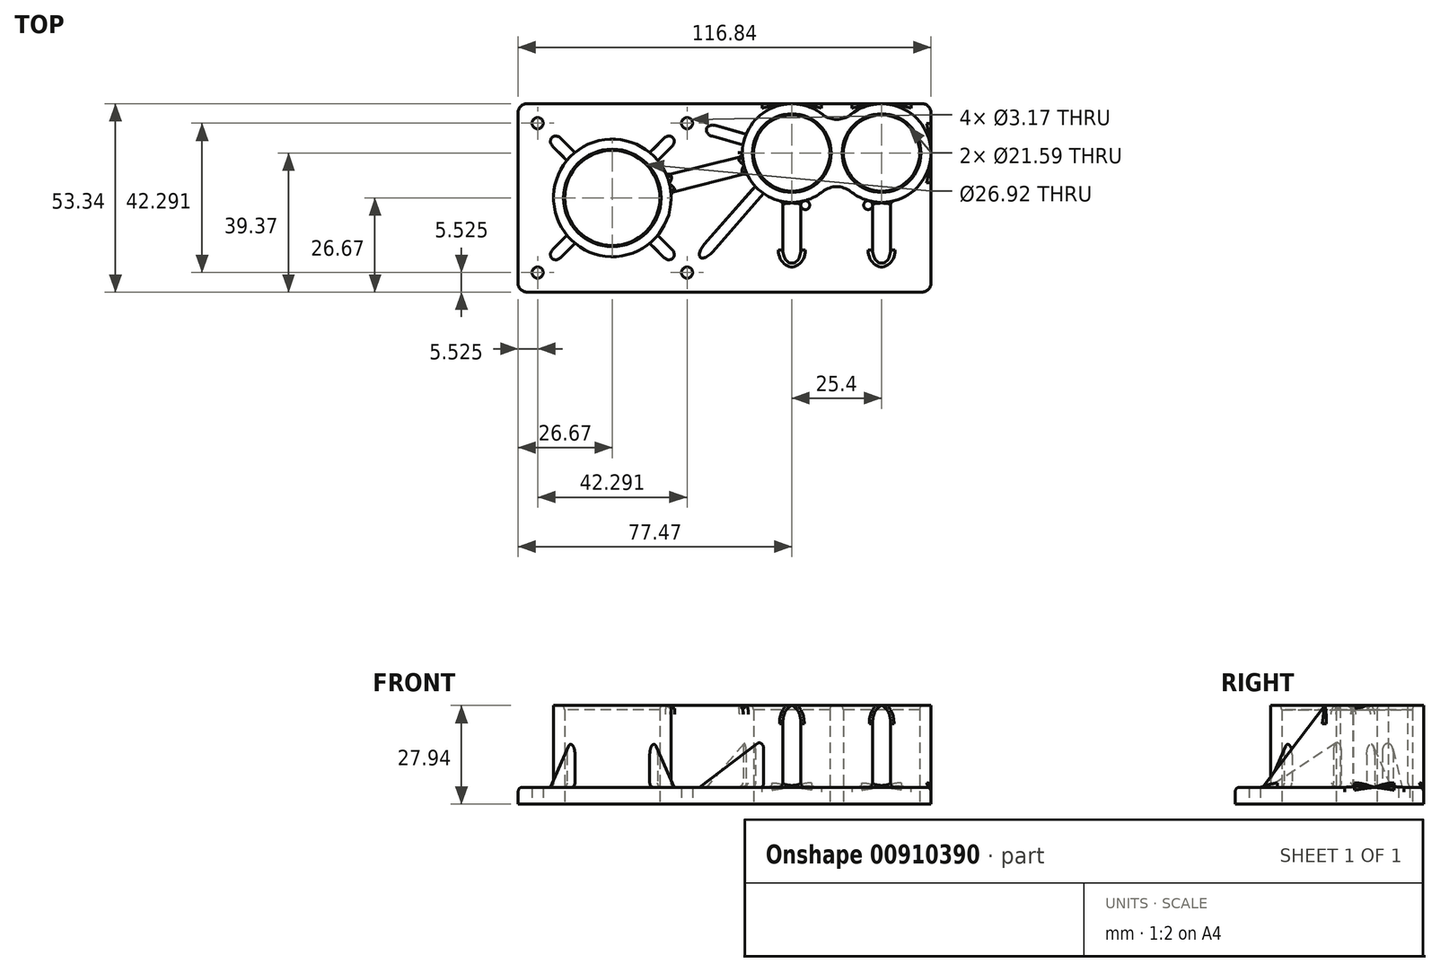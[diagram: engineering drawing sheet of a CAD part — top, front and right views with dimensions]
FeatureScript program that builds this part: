
annotation { "Feature Type Name" : "Feature", "Feature Type Description" : "" }
export const myFeature = defineFeature(function(context is Context, id is Id, definition is map)
    precondition{}
    {
        {
            var Q0;
            Q0=qCreatedBy(makeId("Top.planeOp"),FACE);
            var sketch = newSketch(context, id + "F0", { "sketchPlane" : qUnion([Q0])});
            skCircle(sketch, "E0", {"center": v(0, 0) * mm, "radius": 13.46 * mm});
            skLineSegment(sketch, "E1.bottom", {"start": v(-26.67, 26.67) * mm, "end": v(90.17, 26.67) * mm});
            skLineSegment(sketch, "E1.top", {"start": v(-26.67, -26.67) * mm, "end": v(90.17, -26.67) * mm});
            skLineSegment(sketch, "E1.left", {"start": v(-26.67, 26.67) * mm, "end": v(-26.67, -26.67) * mm});
            skLineSegment(sketch, "E1.right", {"start": v(90.17, 26.67) * mm, "end": v(90.17, -26.67) * mm});
            skCircle(sketch, "E2", {"center": v(50.8, 12.7) * mm, "radius": 10.8 * mm});
            skCircle(sketch, "E3", {"center": v(76.2, 12.7) * mm, "radius": 10.8 * mm});
            skCircle(sketch, "E4", {"center": v(-21.15, 21.15) * mm, "radius": 1.59 * mm});
            skCircle(sketch, "E5", {"center": v(21.15, 21.15) * mm, "radius": 1.59 * mm});
            skCircle(sketch, "E6", {"center": v(21.15, -21.15) * mm, "radius": 1.59 * mm});
            skCircle(sketch, "E7", {"center": v(-21.15, -21.15) * mm, "radius": 1.59 * mm});
            skLineSegment(sketch, "E8", {"start": v(-21.15, 21.15) * mm, "end": v(-21.15, -21.15) * mm, "construction": true});
            skLineSegment(sketch, "E9", {"start": v(21.15, -21.15) * mm, "end": v(21.15, 21.15) * mm, "construction": true});
            skLineSegment(sketch, "E10", {"start": v(21.15, 21.15) * mm, "end": v(-21.15, 21.15) * mm, "construction": true});
            skLineSegment(sketch, "E11", {"start": v(-21.15, -21.15) * mm, "end": v(21.15, -21.15) * mm, "construction": true});
            skLineSegment(sketch, "E12", {"start": v(21.15, -21.15) * mm, "end": v(-21.15, 21.15) * mm, "construction": true});
            skSolve(sketch);
        }
        {
            var Q0;
            Q0 = qSketchRegion(id + "F0", true);
            extrude(context, id + "F1", {"entities" : qUnion([Q0]), "depth" : 4.78 * mm, "offsetDistance" : 25.4 * mm});
        }
        {
            var Q0;
            Q0=qCreatedBy(makeId("Top.planeOp"),FACE);
            var sketch = newSketch(context, id + "F2", { "sketchPlane" : qUnion([Q0])});
            skCircle(sketch, "E13.0", {"center": v(0, 0) * mm, "radius": 13.46 * mm});
            skCircle(sketch, "E13.1", {"center": v(50.8, 12.7) * mm, "radius": 10.8 * mm});
            skCircle(sketch, "E13.2", {"center": v(76.2, 12.7) * mm, "radius": 10.8 * mm});
            skArc(sketch, "E14", {"start": v(15.34, 6.45) * mm, "mid": v(-16.14, -4.04) * mm, "end": v(16.57, 1.52) * mm});
            skArc(sketch, "E15", {"start": v(63.5, 18.52) * mm, "mid": v(47.4, 26.25) * mm, "end": v(36.86, 11.83) * mm});
            skArc(sketch, "E16", {"start": v(63.5, 6.88) * mm, "mid": v(67.61, 1.68) * mm, "end": v(73.66, -1.04) * mm});
            skLineSegment(sketch, "E17", {"start": v(15.34, 6.45) * mm, "end": v(36.86, 11.83) * mm});
            skLineSegment(sketch, "E18", {"start": v(16.57, 1.52) * mm, "end": v(38.09, 6.9) * mm});
            skArc(sketch, "E19.trimOffspring", {"start": v(38.09, 6.9) * mm, "mid": v(42.2, 1.69) * mm, "end": v(48.26, -1.04) * mm});
            skLineSegment(sketch, "E20", {"start": v(48.26, -1.04) * mm, "end": v(48.26, -19.05) * mm});
            skLineSegment(sketch, "E21", {"start": v(48.26, -19.05) * mm, "end": v(53.34, -19.05) * mm});
            skLineSegment(sketch, "E22", {"start": v(53.34, -19.05) * mm, "end": v(53.34, -1.04) * mm});
            skLineSegment(sketch, "E23", {"start": v(73.66, -1.04) * mm, "end": v(73.66, -19.05) * mm});
            skLineSegment(sketch, "E24", {"start": v(73.66, -19.05) * mm, "end": v(78.74, -19.05) * mm});
            skLineSegment(sketch, "E25", {"start": v(78.74, -19.05) * mm, "end": v(78.74, -1.04) * mm});
            skArc(sketch, "E26.trimOffspring", {"start": v(53.34, -1.04) * mm, "mid": v(59.39, 1.68) * mm, "end": v(63.5, 6.88) * mm});
            skArc(sketch, "E27.trimOffspring", {"start": v(78.74, -1.04) * mm, "mid": v(87.22, 21.29) * mm, "end": v(63.5, 18.52) * mm});
            skLineSegment(sketch, "E28", {"start": v(50.8, 12.7) * mm, "end": v(50.8, -19.05) * mm, "construction": true});
            skLineSegment(sketch, "E29", {"start": v(76.2, -19.05) * mm, "end": v(76.2, 12.7) * mm, "construction": true});
            skLineSegment(sketch, "E30", {"start": v(0, 0) * mm, "end": v(50.8, 12.7) * mm, "construction": true});
            skSolve(sketch);
        }
        {
            var Q0;
            Q0 = qSketchRegion(id + "F2", true);
            extrude(context, id + "F3", {"entities" : qUnion([Q0]), "operationType" : NewBodyOperationType.ADD, "depth" : 27.94 * mm, "offsetDistance" : 25.4 * mm});
        }
        {
            var Q0;
            Q0=makeQuery(id+"F3.opExtrude","CAP_EDGE",EDGE,{"disambiguationData":[OSD([sQuery(id+"F2.wireOp",EDGE,"E24")])],"isStart":false});
            var Q1;
            Q1=makeQuery(id+"F3.opExtrude","CAP_EDGE",EDGE,{"disambiguationData":[OSD([sQuery(id+"F2.wireOp",EDGE,"E21")])],"isStart":false});
            chamfer(context, id + "F4", {"entities" : qUnion([Q0, Q1]), "chamferType" : ChamferType.TWO_OFFSETS, "width1" : 17.78 * mm, "oppositeDirection" : false, "width2" : 23.37 * mm, "tangentPropagation" : true});
        }
        {
            var Q0;
            Q0=makeQuery(id+"F1.opExtrude","CAP_FACE",FACE,{"disambiguationData":[OSD([sQuery(id+"F0.wireOp",EDGE,"E0"),sQuery(id+"F0.wireOp",EDGE,"E1.bottom"),sQuery(id+"F0.wireOp",EDGE,"E1.top"),sQuery(id+"F0.wireOp",EDGE,"E1.left"),sQuery(id+"F0.wireOp",EDGE,"E1.right"),sQuery(id+"F0.wireOp",EDGE,"E2"),sQuery(id+"F0.wireOp",EDGE,"E3"),sQuery(id+"F0.wireOp",EDGE,"E4"),sQuery(id+"F0.wireOp",EDGE,"E5"),sQuery(id+"F0.wireOp",EDGE,"E6"),sQuery(id+"F0.wireOp",EDGE,"E7")])],"isStart":false});
            var sketch = newSketch(context, id + "F5", { "sketchPlane" : qUnion([Q0])});
            skLineSegment(sketch, "E31", {"start": v(21.15, 21.15) * mm, "end": v(50.8, 12.7) * mm, "construction": true});
            skLineSegment(sketch, "E32", {"start": v(50.8, 12.7) * mm, "end": v(21.15, -21.15) * mm, "construction": true});
            skLineSegment(sketch, "E33", {"start": v(21.15, -21.15) * mm, "end": v(0, 0) * mm, "construction": true});
            skLineSegment(sketch, "E34", {"start": v(0, 0) * mm, "end": v(-21.15, -21.15) * mm, "construction": true});
            skLineSegment(sketch, "E35", {"start": v(-21.15, 21.15) * mm, "end": v(0, 0) * mm, "construction": true});
            skLineSegment(sketch, "E36", {"start": v(21.15, 21.15) * mm, "end": v(0, 0) * mm, "construction": true});
            skLineSegment(sketch, "E37.bottom", {"start": v(26.1, -17.9) * mm, "end": v(42.85, 1.21) * mm});
            skLineSegment(sketch, "E37.top", {"start": v(23.72, -15.8) * mm, "end": v(40.46, 3.3) * mm});
            skLineSegment(sketch, "E37.left", {"start": v(26.1, -17.9) * mm, "end": v(23.72, -15.8) * mm});
            skLineSegment(sketch, "E37.right", {"start": v(42.85, 1.21) * mm, "end": v(40.46, 3.3) * mm});
            skPoint(sketch, "E37.middle", {"position": v(33.28, -7.3) * mm});
            skLineSegment(sketch, "E38.bottom", {"start": v(10.59, -12.83) * mm, "end": v(15.98, -18.22) * mm});
            skLineSegment(sketch, "E38.top", {"start": v(12.83, -10.59) * mm, "end": v(18.22, -15.98) * mm});
            skLineSegment(sketch, "E38.left", {"start": v(10.59, -12.83) * mm, "end": v(12.83, -10.59) * mm});
            skLineSegment(sketch, "E38.right", {"start": v(15.98, -18.22) * mm, "end": v(18.22, -15.98) * mm});
            skPoint(sketch, "E38.middle", {"position": v(14.4, -14.4) * mm});
            skLineSegment(sketch, "E39.bottom", {"start": v(-15.98, -18.22) * mm, "end": v(-10.59, -12.83) * mm});
            skLineSegment(sketch, "E39.top", {"start": v(-18.22, -15.98) * mm, "end": v(-12.83, -10.59) * mm});
            skLineSegment(sketch, "E39.left", {"start": v(-15.98, -18.22) * mm, "end": v(-18.22, -15.98) * mm});
            skLineSegment(sketch, "E39.right", {"start": v(-10.59, -12.83) * mm, "end": v(-12.83, -10.59) * mm});
            skPoint(sketch, "E39.middle", {"position": v(-14.4, -14.4) * mm});
            skLineSegment(sketch, "E40.bottom", {"start": v(-18.22, 15.98) * mm, "end": v(-12.83, 10.59) * mm});
            skLineSegment(sketch, "E40.top", {"start": v(-15.98, 18.22) * mm, "end": v(-10.59, 12.83) * mm});
            skLineSegment(sketch, "E40.left", {"start": v(-18.22, 15.98) * mm, "end": v(-15.98, 18.22) * mm});
            skLineSegment(sketch, "E40.right", {"start": v(-12.83, 10.59) * mm, "end": v(-10.59, 12.83) * mm});
            skPoint(sketch, "E40.middle", {"position": v(-14.4, 14.4) * mm});
            skLineSegment(sketch, "E41.bottom", {"start": v(12.83, 10.59) * mm, "end": v(18.22, 15.98) * mm});
            skLineSegment(sketch, "E41.top", {"start": v(10.59, 12.83) * mm, "end": v(15.98, 18.22) * mm});
            skLineSegment(sketch, "E41.left", {"start": v(12.83, 10.59) * mm, "end": v(10.59, 12.83) * mm});
            skLineSegment(sketch, "E41.right", {"start": v(18.22, 15.98) * mm, "end": v(15.98, 18.22) * mm});
            skPoint(sketch, "E41.middle", {"position": v(14.4, 14.4) * mm});
            skLineSegment(sketch, "E42.bottom", {"start": v(26.2, 18.05) * mm, "end": v(37.02, 14.97) * mm});
            skLineSegment(sketch, "E42.top", {"start": v(27.08, 21.1) * mm, "end": v(37.89, 18.03) * mm});
            skLineSegment(sketch, "E42.left", {"start": v(26.2, 18.05) * mm, "end": v(27.08, 21.1) * mm});
            skLineSegment(sketch, "E42.right", {"start": v(37.02, 14.97) * mm, "end": v(37.89, 18.03) * mm});
            skPoint(sketch, "E42.middle", {"position": v(32.05, 18.04) * mm});
            skSolve(sketch);
        }
        {
            var Q0;
            Q0 = qSketchRegion(id + "F5", true);
            extrude(context, id + "F6", {"entities" : qUnion([Q0]), "operationType" : NewBodyOperationType.ADD, "depth" : 12.7 * mm, "offsetDistance" : 25.4 * mm});
        }
        {
            var Q0;
            Q0=makeQuery(id+"F6.opExtrude","CAP_EDGE",EDGE,{"disambiguationData":[OSD([sQuery(id+"F5.wireOp",EDGE,"E40.left")])],"isStart":false});
            var Q1;
            Q1=makeQuery(id+"F6.opExtrude","CAP_EDGE",EDGE,{"disambiguationData":[OSD([sQuery(id+"F5.wireOp",EDGE,"E39.left")])],"isStart":false});
            chamfer(context, id + "F7", {"entities" : qUnion([Q0, Q1]), "chamferType" : ChamferType.TWO_OFFSETS, "width1" : 12.7 * mm, "oppositeDirection" : false, "width2" : 7.87 * mm, "tangentPropagation" : true});
        }
        {
            var Q0;
            Q0=makeQuery(id+"F6.opExtrude","CAP_EDGE",EDGE,{"disambiguationData":[OSD([sQuery(id+"F5.wireOp",EDGE,"E41.right")])],"isStart":false});
            var Q1;
            Q1=makeQuery(id+"F6.opExtrude","CAP_EDGE",EDGE,{"disambiguationData":[OSD([sQuery(id+"F5.wireOp",EDGE,"E38.right")])],"isStart":false});
            chamfer(context, id + "F8", {"entities" : qUnion([Q0, Q1]), "chamferType" : ChamferType.TWO_OFFSETS, "width1" : 7.87 * mm, "oppositeDirection" : false, "width2" : 12.7 * mm, "tangentPropagation" : true});
        }
        {
            var Q0;
            Q0=makeQuery(id+"F6.opExtrude","CAP_EDGE",EDGE,{"disambiguationData":[OSD([sQuery(id+"F5.wireOp",EDGE,"E42.left")])],"isStart":false});
            chamfer(context, id + "F9", {"entities" : qUnion([Q0]), "chamferType" : ChamferType.TWO_OFFSETS, "width1" : 12.7 * mm, "oppositeDirection" : false, "width2" : 11.43 * mm, "tangentPropagation" : true});
        }
        {
            var Q0;
            Q0=makeQuery(id+"F6.opExtrude","CAP_EDGE",EDGE,{"disambiguationData":[OSD([sQuery(id+"F5.wireOp",EDGE,"E37.left")])],"isStart":false});
            chamfer(context, id + "F10", {"entities" : qUnion([Q0]), "chamferType" : ChamferType.TWO_OFFSETS, "width1" : 12.7 * mm, "oppositeDirection" : false, "width2" : 25.53 * mm, "tangentPropagation" : true});
        }
        {
            var Q0;
            Q0=makeQuery(id+"F7.opChamfer","BLEND_EDGE",EDGE,{"blendedFrom":[makeQuery(id+"F6.opExtrude","CAP_EDGE",EDGE,{"disambiguationData":[OSD([sQuery(id+"F5.wireOp",EDGE,"E40.left")])],"isStart":false}),makeQuery(id+"F6.opExtrude","SWEPT_FACE",FACE,{"disambiguationData":[OSD([sQuery(id+"F5.wireOp",EDGE,"E40.bottom")])]})],"blendedInto":[makeQuery(id+"F6.opExtrude","SWEPT_FACE",FACE,{"disambiguationData":[OSD([sQuery(id+"F5.wireOp",EDGE,"E40.bottom")])]})]});
            var Q1;
            Q1=makeQuery(id+"F7.opChamfer","BLEND_EDGE",EDGE,{"blendedFrom":[makeQuery(id+"F6.opExtrude","CAP_EDGE",EDGE,{"disambiguationData":[OSD([sQuery(id+"F5.wireOp",EDGE,"E40.left")])],"isStart":false}),makeQuery(id+"F6.opExtrude","SWEPT_FACE",FACE,{"disambiguationData":[OSD([sQuery(id+"F5.wireOp",EDGE,"E40.top")])]})],"blendedInto":[makeQuery(id+"F6.opExtrude","SWEPT_FACE",FACE,{"disambiguationData":[OSD([sQuery(id+"F5.wireOp",EDGE,"E40.top")])]})]});
            var Q2;
            Q2=makeQuery(id+"F7.opChamfer","BLEND_EDGE",EDGE,{"blendedFrom":[makeQuery(id+"F6.opExtrude","CAP_EDGE",EDGE,{"disambiguationData":[OSD([sQuery(id+"F5.wireOp",EDGE,"E39.left")])],"isStart":false}),makeQuery(id+"F6.opExtrude","SWEPT_FACE",FACE,{"disambiguationData":[OSD([sQuery(id+"F5.wireOp",EDGE,"E39.top")])]})],"blendedInto":[makeQuery(id+"F6.opExtrude","SWEPT_FACE",FACE,{"disambiguationData":[OSD([sQuery(id+"F5.wireOp",EDGE,"E39.top")])]})]});
            var Q3;
            Q3=makeQuery(id+"F7.opChamfer","BLEND_EDGE",EDGE,{"blendedFrom":[makeQuery(id+"F6.opExtrude","CAP_EDGE",EDGE,{"disambiguationData":[OSD([sQuery(id+"F5.wireOp",EDGE,"E39.left")])],"isStart":false}),makeQuery(id+"F6.opExtrude","SWEPT_FACE",FACE,{"disambiguationData":[OSD([sQuery(id+"F5.wireOp",EDGE,"E39.bottom")])]})],"blendedInto":[makeQuery(id+"F6.opExtrude","SWEPT_FACE",FACE,{"disambiguationData":[OSD([sQuery(id+"F5.wireOp",EDGE,"E39.bottom")])]})]});
            var Q4;
            Q4=makeQuery(id+"F8.opChamfer","BLEND_EDGE",EDGE,{"blendedFrom":[makeQuery(id+"F6.opExtrude","CAP_EDGE",EDGE,{"disambiguationData":[OSD([sQuery(id+"F5.wireOp",EDGE,"E41.right")])],"isStart":false}),makeQuery(id+"F6.opExtrude","SWEPT_FACE",FACE,{"disambiguationData":[OSD([sQuery(id+"F5.wireOp",EDGE,"E41.top")])]})],"blendedInto":[makeQuery(id+"F6.opExtrude","SWEPT_FACE",FACE,{"disambiguationData":[OSD([sQuery(id+"F5.wireOp",EDGE,"E41.top")])]})]});
            var Q5;
            Q5=makeQuery(id+"F8.opChamfer","BLEND_EDGE",EDGE,{"blendedFrom":[makeQuery(id+"F6.opExtrude","CAP_EDGE",EDGE,{"disambiguationData":[OSD([sQuery(id+"F5.wireOp",EDGE,"E41.right")])],"isStart":false}),makeQuery(id+"F6.opExtrude","SWEPT_FACE",FACE,{"disambiguationData":[OSD([sQuery(id+"F5.wireOp",EDGE,"E41.bottom")])]})],"blendedInto":[makeQuery(id+"F6.opExtrude","SWEPT_FACE",FACE,{"disambiguationData":[OSD([sQuery(id+"F5.wireOp",EDGE,"E41.bottom")])]})]});
            var Q6;
            Q6=makeQuery(id+"F9.opChamfer","BLEND_EDGE",EDGE,{"blendedFrom":[makeQuery(id+"F6.opExtrude","CAP_EDGE",EDGE,{"disambiguationData":[OSD([sQuery(id+"F5.wireOp",EDGE,"E42.left")])],"isStart":false}),makeQuery(id+"F6.opExtrude","SWEPT_FACE",FACE,{"disambiguationData":[OSD([sQuery(id+"F5.wireOp",EDGE,"E42.bottom")])]})],"blendedInto":[makeQuery(id+"F6.opExtrude","SWEPT_FACE",FACE,{"disambiguationData":[OSD([sQuery(id+"F5.wireOp",EDGE,"E42.bottom")])]})]});
            var Q7;
            Q7=makeQuery(id+"F8.opChamfer","BLEND_EDGE",EDGE,{"blendedFrom":[makeQuery(id+"F6.opExtrude","CAP_EDGE",EDGE,{"disambiguationData":[OSD([sQuery(id+"F5.wireOp",EDGE,"E38.right")])],"isStart":false}),makeQuery(id+"F6.opExtrude","SWEPT_FACE",FACE,{"disambiguationData":[OSD([sQuery(id+"F5.wireOp",EDGE,"E38.top")])]})],"blendedInto":[makeQuery(id+"F6.opExtrude","SWEPT_FACE",FACE,{"disambiguationData":[OSD([sQuery(id+"F5.wireOp",EDGE,"E38.top")])]})]});
            var Q8;
            Q8=makeQuery(id+"F8.opChamfer","BLEND_EDGE",EDGE,{"blendedFrom":[makeQuery(id+"F6.opExtrude","CAP_EDGE",EDGE,{"disambiguationData":[OSD([sQuery(id+"F5.wireOp",EDGE,"E38.right")])],"isStart":false}),makeQuery(id+"F6.opExtrude","SWEPT_FACE",FACE,{"disambiguationData":[OSD([sQuery(id+"F5.wireOp",EDGE,"E38.bottom")])]})],"blendedInto":[makeQuery(id+"F6.opExtrude","SWEPT_FACE",FACE,{"disambiguationData":[OSD([sQuery(id+"F5.wireOp",EDGE,"E38.bottom")])]})]});
            var Q9;
            Q9=makeQuery(id+"F10.opChamfer","BLEND_EDGE",EDGE,{"blendedFrom":[makeQuery(id+"F6.opExtrude","CAP_EDGE",EDGE,{"disambiguationData":[OSD([sQuery(id+"F5.wireOp",EDGE,"E37.left")])],"isStart":false}),makeQuery(id+"F6.opExtrude","SWEPT_FACE",FACE,{"disambiguationData":[OSD([sQuery(id+"F5.wireOp",EDGE,"E37.top")])]})],"blendedInto":[makeQuery(id+"F6.opExtrude","SWEPT_FACE",FACE,{"disambiguationData":[OSD([sQuery(id+"F5.wireOp",EDGE,"E37.top")])]})]});
            var Q10;
            Q10=makeQuery(id+"F10.opChamfer","BLEND_EDGE",EDGE,{"blendedFrom":[makeQuery(id+"F6.opExtrude","CAP_EDGE",EDGE,{"disambiguationData":[OSD([sQuery(id+"F5.wireOp",EDGE,"E37.left")])],"isStart":false}),makeQuery(id+"F6.opExtrude","SWEPT_FACE",FACE,{"disambiguationData":[OSD([sQuery(id+"F5.wireOp",EDGE,"E37.bottom")])]})],"blendedInto":[makeQuery(id+"F6.opExtrude","SWEPT_FACE",FACE,{"disambiguationData":[OSD([sQuery(id+"F5.wireOp",EDGE,"E37.bottom")])]})]});
            var Q11;
            Q11=makeQuery(id+"F9.opChamfer","BLEND_EDGE",EDGE,{"blendedFrom":[makeQuery(id+"F6.opExtrude","CAP_EDGE",EDGE,{"disambiguationData":[OSD([sQuery(id+"F5.wireOp",EDGE,"E42.left")])],"isStart":false}),makeQuery(id+"F6.opExtrude","SWEPT_FACE",FACE,{"disambiguationData":[OSD([sQuery(id+"F5.wireOp",EDGE,"E42.top")])]})],"blendedInto":[makeQuery(id+"F6.opExtrude","SWEPT_FACE",FACE,{"disambiguationData":[OSD([sQuery(id+"F5.wireOp",EDGE,"E42.top")])]})]});
            fillet(context, id + "F11", {"entities" : qUnion([Q0, Q1, Q2, Q3, Q4, Q5, Q6, Q7, Q8, Q9, Q10, Q11]), "radius" : 1.59 * mm, "tangentPropagation" : true, "allowEdgeOverflow" : false});
        }
        {
            var Q0;
            Q0=makeQuery(id+"F4.opChamfer","BLEND_EDGE",EDGE,{"blendedFrom":[makeQuery(id+"F3.opExtrude","CAP_EDGE",EDGE,{"disambiguationData":[OSD([sQuery(id+"F2.wireOp",EDGE,"E21")])],"isStart":false}),makeQuery(id+"F3.opExtrude","SWEPT_FACE",FACE,{"disambiguationData":[OSD([sQuery(id+"F2.wireOp",EDGE,"E22")])]})],"blendedInto":[makeQuery(id+"F3.opExtrude","SWEPT_FACE",FACE,{"disambiguationData":[OSD([sQuery(id+"F2.wireOp",EDGE,"E22")])]})]});
            var Q1;
            Q1=makeQuery(id+"F4.opChamfer","BLEND_EDGE",EDGE,{"blendedFrom":[makeQuery(id+"F3.opExtrude","CAP_EDGE",EDGE,{"disambiguationData":[OSD([sQuery(id+"F2.wireOp",EDGE,"E21")])],"isStart":false}),makeQuery(id+"F3.opExtrude","SWEPT_FACE",FACE,{"disambiguationData":[OSD([sQuery(id+"F2.wireOp",EDGE,"E20")])]})],"blendedInto":[makeQuery(id+"F3.opExtrude","SWEPT_FACE",FACE,{"disambiguationData":[OSD([sQuery(id+"F2.wireOp",EDGE,"E20")])]})]});
            var Q2;
            Q2=makeQuery(id+"F4.opChamfer","BLEND_EDGE",EDGE,{"blendedFrom":[makeQuery(id+"F3.opExtrude","CAP_EDGE",EDGE,{"disambiguationData":[OSD([sQuery(id+"F2.wireOp",EDGE,"E24")])],"isStart":false}),makeQuery(id+"F3.opExtrude","SWEPT_FACE",FACE,{"disambiguationData":[OSD([sQuery(id+"F2.wireOp",EDGE,"E23")])]})],"blendedInto":[makeQuery(id+"F3.opExtrude","SWEPT_FACE",FACE,{"disambiguationData":[OSD([sQuery(id+"F2.wireOp",EDGE,"E23")])]})]});
            var Q3;
            Q3=makeQuery(id+"F4.opChamfer","BLEND_EDGE",EDGE,{"blendedFrom":[makeQuery(id+"F3.opExtrude","CAP_EDGE",EDGE,{"disambiguationData":[OSD([sQuery(id+"F2.wireOp",EDGE,"E24")])],"isStart":false}),makeQuery(id+"F3.opExtrude","SWEPT_FACE",FACE,{"disambiguationData":[OSD([sQuery(id+"F2.wireOp",EDGE,"E25")])]})],"blendedInto":[makeQuery(id+"F3.opExtrude","SWEPT_FACE",FACE,{"disambiguationData":[OSD([sQuery(id+"F2.wireOp",EDGE,"E25")])]})]});
            var Q4;
            Q4=makeQuery(id+"F3.opExtrude","CAP_EDGE",EDGE,{"disambiguationData":[OSD([sQuery(id+"F2.wireOp",EDGE,"E17")])],"isStart":false});
            var Q5;
            Q5=makeQuery(id+"F3.opExtrude","CAP_EDGE",EDGE,{"disambiguationData":[OSD([sQuery(id+"F2.wireOp",EDGE,"E18")])],"isStart":false});
            var Q6;
            Q6=makeQuery(id+"F1.opExtrude","SWEPT_EDGE",EDGE,{"disambiguationData":[OSD([sQuery(id+"F0.wireOp",EDGE,"E1.bottom"),sQuery(id+"F0.wireOp",EDGE,"E1.left")])]});
            var Q7;
            Q7=makeQuery(id+"F1.opExtrude","SWEPT_EDGE",EDGE,{"disambiguationData":[OSD([sQuery(id+"F0.wireOp",EDGE,"E1.top"),sQuery(id+"F0.wireOp",EDGE,"E1.left")])]});
            var Q8;
            Q8=makeQuery(id+"F1.opExtrude","SWEPT_EDGE",EDGE,{"disambiguationData":[OSD([sQuery(id+"F0.wireOp",EDGE,"E1.bottom"),sQuery(id+"F0.wireOp",EDGE,"E1.right")])]});
            var Q9;
            Q9=makeQuery(id+"F1.opExtrude","SWEPT_EDGE",EDGE,{"disambiguationData":[OSD([sQuery(id+"F0.wireOp",EDGE,"E1.top"),sQuery(id+"F0.wireOp",EDGE,"E1.right")])]});
            fillet(context, id + "F12", {"entities" : qUnion([Q0, Q1, Q2, Q3, Q4, Q5, Q6, Q7, Q8, Q9]), "radius" : 2.54 * mm, "tangentPropagation" : true, "allowEdgeOverflow" : false});
        }
        {
            var Q0;
            Q0=makeQuery(id+"F3.opExtrude","SWEPT_EDGE",EDGE,{"disambiguationData":[OSD([sQuery(id+"F2.wireOp",EDGE,"E15"),sQuery(id+"F2.wireOp",EDGE,"E27.trimOffspring")])]});
            var Q1;
            Q1=makeQuery(id+"F3.opExtrude","SWEPT_EDGE",EDGE,{"disambiguationData":[OSD([sQuery(id+"F2.wireOp",EDGE,"E16"),sQuery(id+"F2.wireOp",EDGE,"E26.trimOffspring")])]});
            fillet(context, id + "F13", {"entities" : qUnion([Q0, Q1]), "radius" : 6.35 * mm, "tangentPropagation" : true, "allowEdgeOverflow" : false});
        }
        {
            var Q0;
            Q0=makeQuery(id+"F6.opExtrude","SWEPT_EDGE",EDGE,{"disambiguationData":[OSD([sQuery(id+"F0.wireOp",EDGE,"E0"),sQuery(id+"F0.wireOp",EDGE,"E1.bottom"),sQuery(id+"F0.wireOp",EDGE,"E1.top"),sQuery(id+"F0.wireOp",EDGE,"E1.left"),sQuery(id+"F0.wireOp",EDGE,"E1.right"),sQuery(id+"F0.wireOp",EDGE,"E2"),sQuery(id+"F0.wireOp",EDGE,"E3"),sQuery(id+"F0.wireOp",EDGE,"E4"),sQuery(id+"F0.wireOp",EDGE,"E5"),sQuery(id+"F0.wireOp",EDGE,"E6"),sQuery(id+"F0.wireOp",EDGE,"E7"),sQuery(id+"F2.wireOp",EDGE,"E14"),sQuery(id+"F5.wireOp",EDGE,"E41.top"),sQuery(id+"F5.wireOp",EDGE,"E41.left")])]});
            var Q1;
            {var subQ0=makeQuery(id+"F1.opExtrude","CAP_FACE",FACE,{"disambiguationData":[OSD([sQuery(id+"F0.wireOp",EDGE,"E0"),sQuery(id+"F0.wireOp",EDGE,"E1.bottom"),sQuery(id+"F0.wireOp",EDGE,"E1.top"),sQuery(id+"F0.wireOp",EDGE,"E1.left"),sQuery(id+"F0.wireOp",EDGE,"E1.right"),sQuery(id+"F0.wireOp",EDGE,"E2"),sQuery(id+"F0.wireOp",EDGE,"E3"),sQuery(id+"F0.wireOp",EDGE,"E4"),sQuery(id+"F0.wireOp",EDGE,"E5"),sQuery(id+"F0.wireOp",EDGE,"E6"),sQuery(id+"F0.wireOp",EDGE,"E7")])],"isStart":false});var subQ1=makeQuery(id+"F3.opExtrude","SWEPT_FACE",FACE,{"disambiguationData":[OSD([sQuery(id+"F2.wireOp",EDGE,"E14")])]});Q1=makeQuery(id+"F6.boolean.opBoolean","SPLIT",EDGE,{"disambiguationData":[TD([makeQuery(id+"F6.opExtrude","SWEPT_FACE",FACE,{"disambiguationData":[OSD([sQuery(id+"F5.wireOp",EDGE,"E40.top")])]})])],"derivedFrom":makeQuery(id+"F3.boolean.opBoolean","INTERSECT",EDGE,{"derivedFrom":[subQ0,subQ1]})});}
            var Q2;
            Q2=makeQuery(id+"F6.opExtrude","CAP_EDGE",EDGE,{"disambiguationData":[OSD([sQuery(id+"F5.wireOp",EDGE,"E41.top")])],"isStart":true});
            var Q3;
            Q3=makeQuery(id+"F6.opExtrude","CAP_EDGE",EDGE,{"disambiguationData":[OSD([sQuery(id+"F5.wireOp",EDGE,"E40.top")])],"isStart":true});
            var Q4;
            {var subQ0=makeQuery(id+"F1.opExtrude","CAP_FACE",FACE,{"disambiguationData":[OSD([sQuery(id+"F0.wireOp",EDGE,"E0"),sQuery(id+"F0.wireOp",EDGE,"E1.bottom"),sQuery(id+"F0.wireOp",EDGE,"E1.top"),sQuery(id+"F0.wireOp",EDGE,"E1.left"),sQuery(id+"F0.wireOp",EDGE,"E1.right"),sQuery(id+"F0.wireOp",EDGE,"E2"),sQuery(id+"F0.wireOp",EDGE,"E3"),sQuery(id+"F0.wireOp",EDGE,"E4"),sQuery(id+"F0.wireOp",EDGE,"E5"),sQuery(id+"F0.wireOp",EDGE,"E6"),sQuery(id+"F0.wireOp",EDGE,"E7")])],"isStart":false});var subQ1=makeQuery(id+"F3.opExtrude","SWEPT_FACE",FACE,{"disambiguationData":[OSD([sQuery(id+"F2.wireOp",EDGE,"E14")])]});Q4=makeQuery(id+"F6.boolean.opBoolean","SPLIT",EDGE,{"disambiguationData":[TD([makeQuery(id+"F6.opExtrude","SWEPT_FACE",FACE,{"disambiguationData":[OSD([sQuery(id+"F5.wireOp",EDGE,"E39.top")])]})])],"derivedFrom":makeQuery(id+"F3.boolean.opBoolean","INTERSECT",EDGE,{"derivedFrom":[subQ0,subQ1]})});}
            var Q5;
            Q5=makeQuery(id+"F6.opExtrude","SWEPT_EDGE",EDGE,{"disambiguationData":[OSD([sQuery(id+"F0.wireOp",EDGE,"E0"),sQuery(id+"F0.wireOp",EDGE,"E1.bottom"),sQuery(id+"F0.wireOp",EDGE,"E1.top"),sQuery(id+"F0.wireOp",EDGE,"E1.left"),sQuery(id+"F0.wireOp",EDGE,"E1.right"),sQuery(id+"F0.wireOp",EDGE,"E2"),sQuery(id+"F0.wireOp",EDGE,"E3"),sQuery(id+"F0.wireOp",EDGE,"E4"),sQuery(id+"F0.wireOp",EDGE,"E5"),sQuery(id+"F0.wireOp",EDGE,"E6"),sQuery(id+"F0.wireOp",EDGE,"E7"),sQuery(id+"F2.wireOp",EDGE,"E14"),sQuery(id+"F5.wireOp",EDGE,"E40.bottom"),sQuery(id+"F5.wireOp",EDGE,"E40.right")])]});
            var Q6;
            Q6=makeQuery(id+"F6.opExtrude","SWEPT_EDGE",EDGE,{"disambiguationData":[OSD([sQuery(id+"F0.wireOp",EDGE,"E0"),sQuery(id+"F0.wireOp",EDGE,"E1.bottom"),sQuery(id+"F0.wireOp",EDGE,"E1.top"),sQuery(id+"F0.wireOp",EDGE,"E1.left"),sQuery(id+"F0.wireOp",EDGE,"E1.right"),sQuery(id+"F0.wireOp",EDGE,"E2"),sQuery(id+"F0.wireOp",EDGE,"E3"),sQuery(id+"F0.wireOp",EDGE,"E4"),sQuery(id+"F0.wireOp",EDGE,"E5"),sQuery(id+"F0.wireOp",EDGE,"E6"),sQuery(id+"F0.wireOp",EDGE,"E7"),sQuery(id+"F2.wireOp",EDGE,"E14"),sQuery(id+"F5.wireOp",EDGE,"E39.top"),sQuery(id+"F5.wireOp",EDGE,"E39.right")])]});
            var Q7;
            Q7=makeQuery(id+"F6.opExtrude","CAP_EDGE",EDGE,{"disambiguationData":[OSD([sQuery(id+"F5.wireOp",EDGE,"E39.top")])],"isStart":true});
            var Q8;
            {var subQ0=makeQuery(id+"F1.opExtrude","CAP_FACE",FACE,{"disambiguationData":[OSD([sQuery(id+"F0.wireOp",EDGE,"E0"),sQuery(id+"F0.wireOp",EDGE,"E1.bottom"),sQuery(id+"F0.wireOp",EDGE,"E1.top"),sQuery(id+"F0.wireOp",EDGE,"E1.left"),sQuery(id+"F0.wireOp",EDGE,"E1.right"),sQuery(id+"F0.wireOp",EDGE,"E2"),sQuery(id+"F0.wireOp",EDGE,"E3"),sQuery(id+"F0.wireOp",EDGE,"E4"),sQuery(id+"F0.wireOp",EDGE,"E5"),sQuery(id+"F0.wireOp",EDGE,"E6"),sQuery(id+"F0.wireOp",EDGE,"E7")])],"isStart":false});var subQ1=makeQuery(id+"F3.opExtrude","SWEPT_FACE",FACE,{"disambiguationData":[OSD([sQuery(id+"F2.wireOp",EDGE,"E14")])]});Q8=makeQuery(id+"F6.boolean.opBoolean","SPLIT",EDGE,{"disambiguationData":[TD([makeQuery(id+"F6.opExtrude","SWEPT_FACE",FACE,{"disambiguationData":[OSD([sQuery(id+"F5.wireOp",EDGE,"E38.bottom")])]})])],"derivedFrom":makeQuery(id+"F3.boolean.opBoolean","INTERSECT",EDGE,{"derivedFrom":[subQ0,subQ1]})});}
            var Q9;
            Q9=makeQuery(id+"F6.opExtrude","SWEPT_EDGE",EDGE,{"disambiguationData":[OSD([sQuery(id+"F0.wireOp",EDGE,"E0"),sQuery(id+"F0.wireOp",EDGE,"E1.bottom"),sQuery(id+"F0.wireOp",EDGE,"E1.top"),sQuery(id+"F0.wireOp",EDGE,"E1.left"),sQuery(id+"F0.wireOp",EDGE,"E1.right"),sQuery(id+"F0.wireOp",EDGE,"E2"),sQuery(id+"F0.wireOp",EDGE,"E3"),sQuery(id+"F0.wireOp",EDGE,"E4"),sQuery(id+"F0.wireOp",EDGE,"E5"),sQuery(id+"F0.wireOp",EDGE,"E6"),sQuery(id+"F0.wireOp",EDGE,"E7"),sQuery(id+"F2.wireOp",EDGE,"E14"),sQuery(id+"F5.wireOp",EDGE,"E38.bottom"),sQuery(id+"F5.wireOp",EDGE,"E38.left")])]});
            var Q10;
            Q10=makeQuery(id+"F6.opExtrude","CAP_EDGE",EDGE,{"disambiguationData":[OSD([sQuery(id+"F5.wireOp",EDGE,"E38.bottom")])],"isStart":true});
            var Q11;
            {var subQ0=makeQuery(id+"F1.opExtrude","CAP_FACE",FACE,{"disambiguationData":[OSD([sQuery(id+"F0.wireOp",EDGE,"E0"),sQuery(id+"F0.wireOp",EDGE,"E1.bottom"),sQuery(id+"F0.wireOp",EDGE,"E1.top"),sQuery(id+"F0.wireOp",EDGE,"E1.left"),sQuery(id+"F0.wireOp",EDGE,"E1.right"),sQuery(id+"F0.wireOp",EDGE,"E2"),sQuery(id+"F0.wireOp",EDGE,"E3"),sQuery(id+"F0.wireOp",EDGE,"E4"),sQuery(id+"F0.wireOp",EDGE,"E5"),sQuery(id+"F0.wireOp",EDGE,"E6"),sQuery(id+"F0.wireOp",EDGE,"E7")])],"isStart":false});var subQ1=makeQuery(id+"F3.opExtrude","SWEPT_FACE",FACE,{"disambiguationData":[OSD([sQuery(id+"F2.wireOp",EDGE,"E14")])]});Q11=makeQuery(id+"F6.boolean.opBoolean","SPLIT",EDGE,{"disambiguationData":[TD([makeQuery(id+"F3.opExtrude","SWEPT_FACE",FACE,{"disambiguationData":[OSD([sQuery(id+"F2.wireOp",EDGE,"E18")])]})])],"derivedFrom":makeQuery(id+"F3.boolean.opBoolean","INTERSECT",EDGE,{"derivedFrom":[subQ0,subQ1]})});}
            var Q12;
            Q12=makeQuery(id+"F3.opExtrude","SWEPT_EDGE",EDGE,{"disambiguationData":[OSD([sQuery(id+"F2.wireOp",EDGE,"E14"),sQuery(id+"F2.wireOp",EDGE,"E18")])]});
            var Q13;
            Q13=makeQuery(id+"F3.opExtrude","SWEPT_EDGE",EDGE,{"disambiguationData":[OSD([sQuery(id+"F2.wireOp",EDGE,"E18"),sQuery(id+"F2.wireOp",EDGE,"E19.trimOffspring")])]});
            var Q14;
            {var subQ0=makeQuery(id+"F1.opExtrude","CAP_FACE",FACE,{"disambiguationData":[OSD([sQuery(id+"F0.wireOp",EDGE,"E0"),sQuery(id+"F0.wireOp",EDGE,"E1.bottom"),sQuery(id+"F0.wireOp",EDGE,"E1.top"),sQuery(id+"F0.wireOp",EDGE,"E1.left"),sQuery(id+"F0.wireOp",EDGE,"E1.right"),sQuery(id+"F0.wireOp",EDGE,"E2"),sQuery(id+"F0.wireOp",EDGE,"E3"),sQuery(id+"F0.wireOp",EDGE,"E4"),sQuery(id+"F0.wireOp",EDGE,"E5"),sQuery(id+"F0.wireOp",EDGE,"E6"),sQuery(id+"F0.wireOp",EDGE,"E7")])],"isStart":false});var subQ1=makeQuery(id+"F3.opExtrude","SWEPT_FACE",FACE,{"disambiguationData":[OSD([sQuery(id+"F2.wireOp",EDGE,"E19.trimOffspring")])]});Q14=makeQuery(id+"F6.boolean.opBoolean","SPLIT",EDGE,{"disambiguationData":[TD([makeQuery(id+"F3.opExtrude","SWEPT_FACE",FACE,{"disambiguationData":[OSD([sQuery(id+"F2.wireOp",EDGE,"E18")])]})])],"derivedFrom":makeQuery(id+"F3.boolean.opBoolean","INTERSECT",EDGE,{"derivedFrom":[subQ0,subQ1]})});}
            var Q15;
            Q15=makeQuery(id+"F6.opExtrude","CAP_EDGE",EDGE,{"disambiguationData":[OSD([sQuery(id+"F5.wireOp",EDGE,"E37.top")])],"isStart":true});
            var Q16;
            Q16=makeQuery(id+"F6.opExtrude","SWEPT_EDGE",EDGE,{"disambiguationData":[OSD([sQuery(id+"F0.wireOp",EDGE,"E0"),sQuery(id+"F0.wireOp",EDGE,"E1.bottom"),sQuery(id+"F0.wireOp",EDGE,"E1.top"),sQuery(id+"F0.wireOp",EDGE,"E1.left"),sQuery(id+"F0.wireOp",EDGE,"E1.right"),sQuery(id+"F0.wireOp",EDGE,"E2"),sQuery(id+"F0.wireOp",EDGE,"E3"),sQuery(id+"F0.wireOp",EDGE,"E4"),sQuery(id+"F0.wireOp",EDGE,"E5"),sQuery(id+"F0.wireOp",EDGE,"E6"),sQuery(id+"F0.wireOp",EDGE,"E7"),sQuery(id+"F2.wireOp",EDGE,"E19.trimOffspring"),sQuery(id+"F5.wireOp",EDGE,"E37.bottom"),sQuery(id+"F5.wireOp",EDGE,"E37.right")])]});
            var Q17;
            Q17=makeQuery(id+"F3.opExtrude","SWEPT_EDGE",EDGE,{"disambiguationData":[OSD([sQuery(id+"F2.wireOp",EDGE,"E22"),sQuery(id+"F2.wireOp",EDGE,"E26.trimOffspring")])]});
            var Q18;
            Q18=makeQuery(id+"F3.boolean.opBoolean","INTERSECT",EDGE,{"derivedFrom":[makeQuery(id+"F1.opExtrude","CAP_FACE",FACE,{"disambiguationData":[OSD([sQuery(id+"F0.wireOp",EDGE,"E0"),sQuery(id+"F0.wireOp",EDGE,"E1.bottom"),sQuery(id+"F0.wireOp",EDGE,"E1.top"),sQuery(id+"F0.wireOp",EDGE,"E1.left"),sQuery(id+"F0.wireOp",EDGE,"E1.right"),sQuery(id+"F0.wireOp",EDGE,"E2"),sQuery(id+"F0.wireOp",EDGE,"E3"),sQuery(id+"F0.wireOp",EDGE,"E4"),sQuery(id+"F0.wireOp",EDGE,"E5"),sQuery(id+"F0.wireOp",EDGE,"E6"),sQuery(id+"F0.wireOp",EDGE,"E7")])],"isStart":false}),makeQuery(id+"F3.opExtrude","SWEPT_FACE",FACE,{"disambiguationData":[OSD([sQuery(id+"F2.wireOp",EDGE,"E22")])]})]});
            var Q19;
            {var subQ0=makeQuery(id+"F1.opExtrude","CAP_FACE",FACE,{"disambiguationData":[OSD([sQuery(id+"F0.wireOp",EDGE,"E0"),sQuery(id+"F0.wireOp",EDGE,"E1.bottom"),sQuery(id+"F0.wireOp",EDGE,"E1.top"),sQuery(id+"F0.wireOp",EDGE,"E1.left"),sQuery(id+"F0.wireOp",EDGE,"E1.right"),sQuery(id+"F0.wireOp",EDGE,"E2"),sQuery(id+"F0.wireOp",EDGE,"E3"),sQuery(id+"F0.wireOp",EDGE,"E4"),sQuery(id+"F0.wireOp",EDGE,"E5"),sQuery(id+"F0.wireOp",EDGE,"E6"),sQuery(id+"F0.wireOp",EDGE,"E7")])],"isStart":false});var subQ1=makeQuery(id+"F3.opExtrude","SWEPT_FACE",FACE,{"disambiguationData":[OSD([sQuery(id+"F2.wireOp",EDGE,"E19.trimOffspring")])]});Q19=makeQuery(id+"F6.boolean.opBoolean","SPLIT",EDGE,{"disambiguationData":[TD([makeQuery(id+"F3.opExtrude","SWEPT_FACE",FACE,{"disambiguationData":[OSD([sQuery(id+"F2.wireOp",EDGE,"E20")])]})])],"derivedFrom":makeQuery(id+"F3.boolean.opBoolean","INTERSECT",EDGE,{"derivedFrom":[subQ0,subQ1]})});}
            var Q20;
            Q20=makeQuery(id+"F3.boolean.opBoolean","INTERSECT",EDGE,{"derivedFrom":[makeQuery(id+"F1.opExtrude","CAP_FACE",FACE,{"disambiguationData":[OSD([sQuery(id+"F0.wireOp",EDGE,"E0"),sQuery(id+"F0.wireOp",EDGE,"E1.bottom"),sQuery(id+"F0.wireOp",EDGE,"E1.top"),sQuery(id+"F0.wireOp",EDGE,"E1.left"),sQuery(id+"F0.wireOp",EDGE,"E1.right"),sQuery(id+"F0.wireOp",EDGE,"E2"),sQuery(id+"F0.wireOp",EDGE,"E3"),sQuery(id+"F0.wireOp",EDGE,"E4"),sQuery(id+"F0.wireOp",EDGE,"E5"),sQuery(id+"F0.wireOp",EDGE,"E6"),sQuery(id+"F0.wireOp",EDGE,"E7")])],"isStart":false}),makeQuery(id+"F3.opExtrude","SWEPT_FACE",FACE,{"disambiguationData":[OSD([sQuery(id+"F2.wireOp",EDGE,"E26.trimOffspring")])]})]});
            var Q21;
            Q21=makeQuery(id+"F3.opExtrude","SWEPT_EDGE",EDGE,{"disambiguationData":[OSD([sQuery(id+"F2.wireOp",EDGE,"E19.trimOffspring"),sQuery(id+"F2.wireOp",EDGE,"E20")])]});
            var Q22;
            Q22=makeQuery(id+"F3.opExtrude","SWEPT_EDGE",EDGE,{"disambiguationData":[OSD([sQuery(id+"F2.wireOp",EDGE,"E25"),sQuery(id+"F2.wireOp",EDGE,"E27.trimOffspring")])]});
            var Q23;
            Q23=makeQuery(id+"F3.boolean.opBoolean","INTERSECT",EDGE,{"derivedFrom":[makeQuery(id+"F1.opExtrude","CAP_FACE",FACE,{"disambiguationData":[OSD([sQuery(id+"F0.wireOp",EDGE,"E0"),sQuery(id+"F0.wireOp",EDGE,"E1.bottom"),sQuery(id+"F0.wireOp",EDGE,"E1.top"),sQuery(id+"F0.wireOp",EDGE,"E1.left"),sQuery(id+"F0.wireOp",EDGE,"E1.right"),sQuery(id+"F0.wireOp",EDGE,"E2"),sQuery(id+"F0.wireOp",EDGE,"E3"),sQuery(id+"F0.wireOp",EDGE,"E4"),sQuery(id+"F0.wireOp",EDGE,"E5"),sQuery(id+"F0.wireOp",EDGE,"E6"),sQuery(id+"F0.wireOp",EDGE,"E7")])],"isStart":false}),makeQuery(id+"F3.opExtrude","SWEPT_FACE",FACE,{"disambiguationData":[OSD([sQuery(id+"F2.wireOp",EDGE,"E25")])]})]});
            var Q24;
            Q24=makeQuery(id+"F3.boolean.opBoolean","INTERSECT",EDGE,{"derivedFrom":[makeQuery(id+"F1.opExtrude","CAP_FACE",FACE,{"disambiguationData":[OSD([sQuery(id+"F0.wireOp",EDGE,"E0"),sQuery(id+"F0.wireOp",EDGE,"E1.bottom"),sQuery(id+"F0.wireOp",EDGE,"E1.top"),sQuery(id+"F0.wireOp",EDGE,"E1.left"),sQuery(id+"F0.wireOp",EDGE,"E1.right"),sQuery(id+"F0.wireOp",EDGE,"E2"),sQuery(id+"F0.wireOp",EDGE,"E3"),sQuery(id+"F0.wireOp",EDGE,"E4"),sQuery(id+"F0.wireOp",EDGE,"E5"),sQuery(id+"F0.wireOp",EDGE,"E6"),sQuery(id+"F0.wireOp",EDGE,"E7")])],"isStart":false}),makeQuery(id+"F3.opExtrude","SWEPT_FACE",FACE,{"disambiguationData":[OSD([sQuery(id+"F2.wireOp",EDGE,"E27.trimOffspring")])]})]});
            var Q25;
            Q25=makeQuery(id+"F3.opExtrude","SWEPT_EDGE",EDGE,{"disambiguationData":[OSD([sQuery(id+"F2.wireOp",EDGE,"E16"),sQuery(id+"F2.wireOp",EDGE,"E23")])]});
            var Q26;
            Q26=makeQuery(id+"F6.opExtrude","SWEPT_EDGE",EDGE,{"disambiguationData":[OSD([sQuery(id+"F0.wireOp",EDGE,"E0"),sQuery(id+"F0.wireOp",EDGE,"E1.bottom"),sQuery(id+"F0.wireOp",EDGE,"E1.top"),sQuery(id+"F0.wireOp",EDGE,"E1.left"),sQuery(id+"F0.wireOp",EDGE,"E1.right"),sQuery(id+"F0.wireOp",EDGE,"E2"),sQuery(id+"F0.wireOp",EDGE,"E3"),sQuery(id+"F0.wireOp",EDGE,"E4"),sQuery(id+"F0.wireOp",EDGE,"E5"),sQuery(id+"F0.wireOp",EDGE,"E6"),sQuery(id+"F0.wireOp",EDGE,"E7"),sQuery(id+"F2.wireOp",EDGE,"E15"),sQuery(id+"F5.wireOp",EDGE,"E42.top"),sQuery(id+"F5.wireOp",EDGE,"E42.right")])]});
            var Q27;
            Q27=makeQuery(id+"F6.opExtrude","CAP_EDGE",EDGE,{"disambiguationData":[OSD([sQuery(id+"F5.wireOp",EDGE,"E42.top")])],"isStart":true});
            var Q28;
            {var subQ0=makeQuery(id+"F1.opExtrude","CAP_FACE",FACE,{"disambiguationData":[OSD([sQuery(id+"F0.wireOp",EDGE,"E0"),sQuery(id+"F0.wireOp",EDGE,"E1.bottom"),sQuery(id+"F0.wireOp",EDGE,"E1.top"),sQuery(id+"F0.wireOp",EDGE,"E1.left"),sQuery(id+"F0.wireOp",EDGE,"E1.right"),sQuery(id+"F0.wireOp",EDGE,"E2"),sQuery(id+"F0.wireOp",EDGE,"E3"),sQuery(id+"F0.wireOp",EDGE,"E4"),sQuery(id+"F0.wireOp",EDGE,"E5"),sQuery(id+"F0.wireOp",EDGE,"E6"),sQuery(id+"F0.wireOp",EDGE,"E7")])],"isStart":false});var subQ1=makeQuery(id+"F3.opExtrude","SWEPT_FACE",FACE,{"disambiguationData":[OSD([sQuery(id+"F2.wireOp",EDGE,"E15")])]});Q28=makeQuery(id+"F6.boolean.opBoolean","SPLIT",EDGE,{"disambiguationData":[TD([makeQuery(id+"F3.opExtrude","SWEPT_FACE",FACE,{"disambiguationData":[OSD([sQuery(id+"F2.wireOp",EDGE,"E17")])]})])],"derivedFrom":makeQuery(id+"F3.boolean.opBoolean","INTERSECT",EDGE,{"derivedFrom":[subQ0,subQ1]})});}
            var Q29;
            Q29=makeQuery(id+"F3.boolean.opBoolean","INTERSECT",EDGE,{"derivedFrom":[makeQuery(id+"F1.opExtrude","CAP_FACE",FACE,{"disambiguationData":[OSD([sQuery(id+"F0.wireOp",EDGE,"E0"),sQuery(id+"F0.wireOp",EDGE,"E1.bottom"),sQuery(id+"F0.wireOp",EDGE,"E1.top"),sQuery(id+"F0.wireOp",EDGE,"E1.left"),sQuery(id+"F0.wireOp",EDGE,"E1.right"),sQuery(id+"F0.wireOp",EDGE,"E2"),sQuery(id+"F0.wireOp",EDGE,"E3"),sQuery(id+"F0.wireOp",EDGE,"E4"),sQuery(id+"F0.wireOp",EDGE,"E5"),sQuery(id+"F0.wireOp",EDGE,"E6"),sQuery(id+"F0.wireOp",EDGE,"E7")])],"isStart":false}),makeQuery(id+"F3.opExtrude","SWEPT_FACE",FACE,{"disambiguationData":[OSD([sQuery(id+"F2.wireOp",EDGE,"E17")])]})]});
            var Q30;
            {var subQ0=makeQuery(id+"F1.opExtrude","CAP_FACE",FACE,{"disambiguationData":[OSD([sQuery(id+"F0.wireOp",EDGE,"E0"),sQuery(id+"F0.wireOp",EDGE,"E1.bottom"),sQuery(id+"F0.wireOp",EDGE,"E1.top"),sQuery(id+"F0.wireOp",EDGE,"E1.left"),sQuery(id+"F0.wireOp",EDGE,"E1.right"),sQuery(id+"F0.wireOp",EDGE,"E2"),sQuery(id+"F0.wireOp",EDGE,"E3"),sQuery(id+"F0.wireOp",EDGE,"E4"),sQuery(id+"F0.wireOp",EDGE,"E5"),sQuery(id+"F0.wireOp",EDGE,"E6"),sQuery(id+"F0.wireOp",EDGE,"E7")])],"isStart":false});var subQ1=makeQuery(id+"F3.opExtrude","SWEPT_FACE",FACE,{"disambiguationData":[OSD([sQuery(id+"F2.wireOp",EDGE,"E14")])]});Q30=makeQuery(id+"F6.boolean.opBoolean","SPLIT",EDGE,{"disambiguationData":[TD([makeQuery(id+"F3.opExtrude","SWEPT_FACE",FACE,{"disambiguationData":[OSD([sQuery(id+"F2.wireOp",EDGE,"E17")])]})])],"derivedFrom":makeQuery(id+"F3.boolean.opBoolean","INTERSECT",EDGE,{"derivedFrom":[subQ0,subQ1]})});}
            fillet(context, id + "F14", {"entities" : qUnion([Q0, Q1, Q2, Q3, Q4, Q5, Q6, Q7, Q8, Q9, Q10, Q11, Q12, Q13, Q14, Q15, Q16, Q17, Q18, Q19, Q20, Q21, Q22, Q23, Q24, Q25, Q26, Q27, Q28, Q29, Q30]), "radius" : 1.27 * mm, "tangentPropagation" : true, "allowEdgeOverflow" : false});
        }
        {
            var Q0;
            Q0=makeQuery(id+"F1.opExtrude","CAP_EDGE",EDGE,{"disambiguationData":[OSD([sQuery(id+"F0.wireOp",EDGE,"E1.bottom")])],"isStart":false});
            fillet(context, id + "F15", {"entities" : qUnion([Q0]), "radius" : 1.27 * mm, "tangentPropagation" : true, "allowEdgeOverflow" : false});
        }
        {
            var Q0;
            Q0=makeQuery(id+"F3.opExtrude","CAP_EDGE",EDGE,{"disambiguationData":[OSD([sQuery(id+"F2.wireOp",EDGE,"E13.2")])],"isStart":false});
            var Q1;
            Q1=makeQuery(id+"F3.opExtrude","CAP_EDGE",EDGE,{"disambiguationData":[OSD([sQuery(id+"F2.wireOp",EDGE,"E13.1")])],"isStart":false});
            var Q2;
            Q2=makeQuery(id+"F3.opExtrude","CAP_EDGE",EDGE,{"disambiguationData":[OSD([sQuery(id+"F2.wireOp",EDGE,"E13.0")])],"isStart":false});
            chamfer(context, id + "F16", {"entities" : qUnion([Q0, Q1, Q2]), "chamferType" : ChamferType.OFFSET_ANGLE, "width" : 1.27 * mm, "oppositeDirection" : false, "angle" : 15 * degree, "tangentPropagation" : true});
        }
    });
